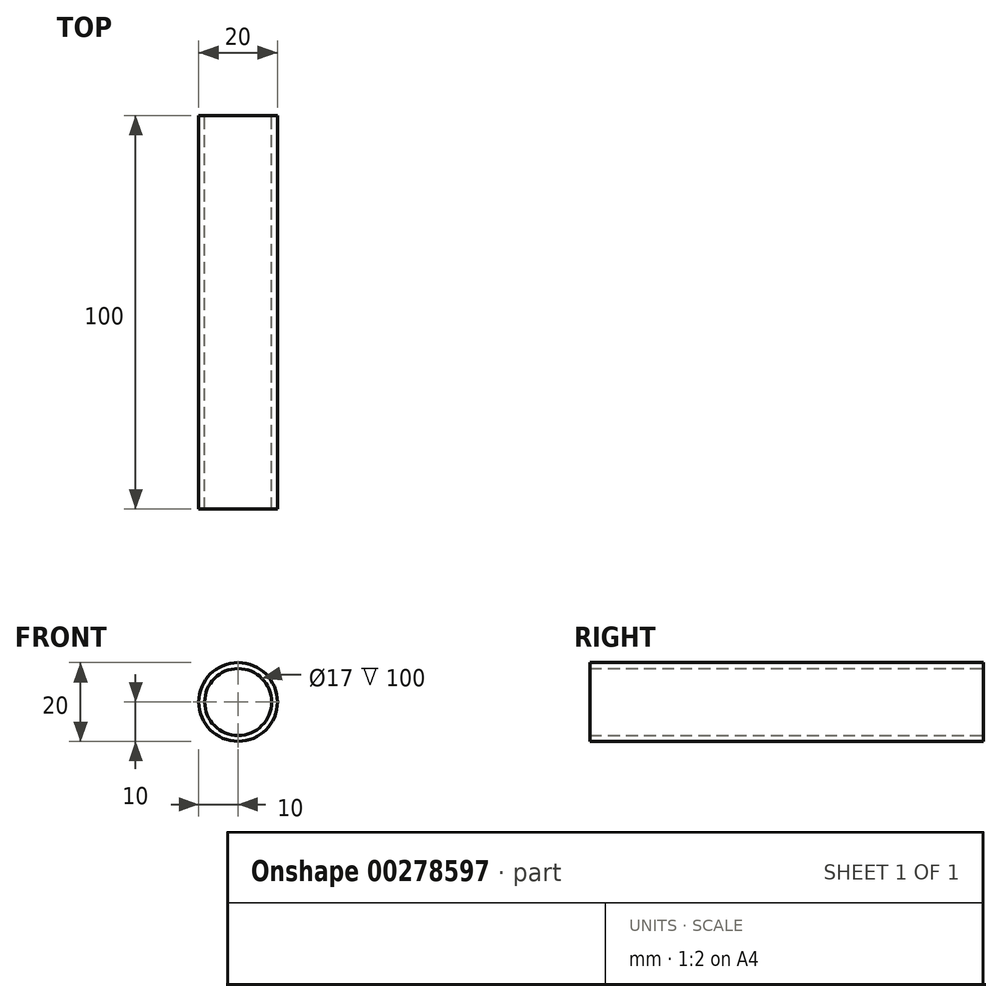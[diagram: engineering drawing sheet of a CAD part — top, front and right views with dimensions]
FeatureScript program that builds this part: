
annotation { "Feature Type Name" : "Feature", "Feature Type Description" : "" }
export const myFeature = defineFeature(function(context is Context, id is Id, definition is map)
    precondition{}
    {
        {
            var Q0;
            Q0=qCreatedBy(makeId("Front.planeOp"),FACE);
            var sketch = newSketch(context, id + "F0", { "sketchPlane" : qUnion([Q0])});
            skCircle(sketch, "E0", {"center": v(0, 0) * mm, "radius": 10 * mm});
            skCircle(sketch, "E1", {"center": v(0, 0) * mm, "radius": 8.5 * mm});
            skSolve(sketch);
        }
        {
            var Q0;
            Q0=makeQuery(id+"F0.imprint","IMPRINT",FACE,{"disambiguationData":[TD([[makeQuery(id+"F0.imprint","IMPRINT",EDGE,{"derivedFrom":sQuery(id+"F0.wireOp",EDGE,"E0")}),1.0]])]});
            extrude(context, id + "F1", {"entities" : qUnion([Q0]), "depth" : 100 * mm});
        }
    });
